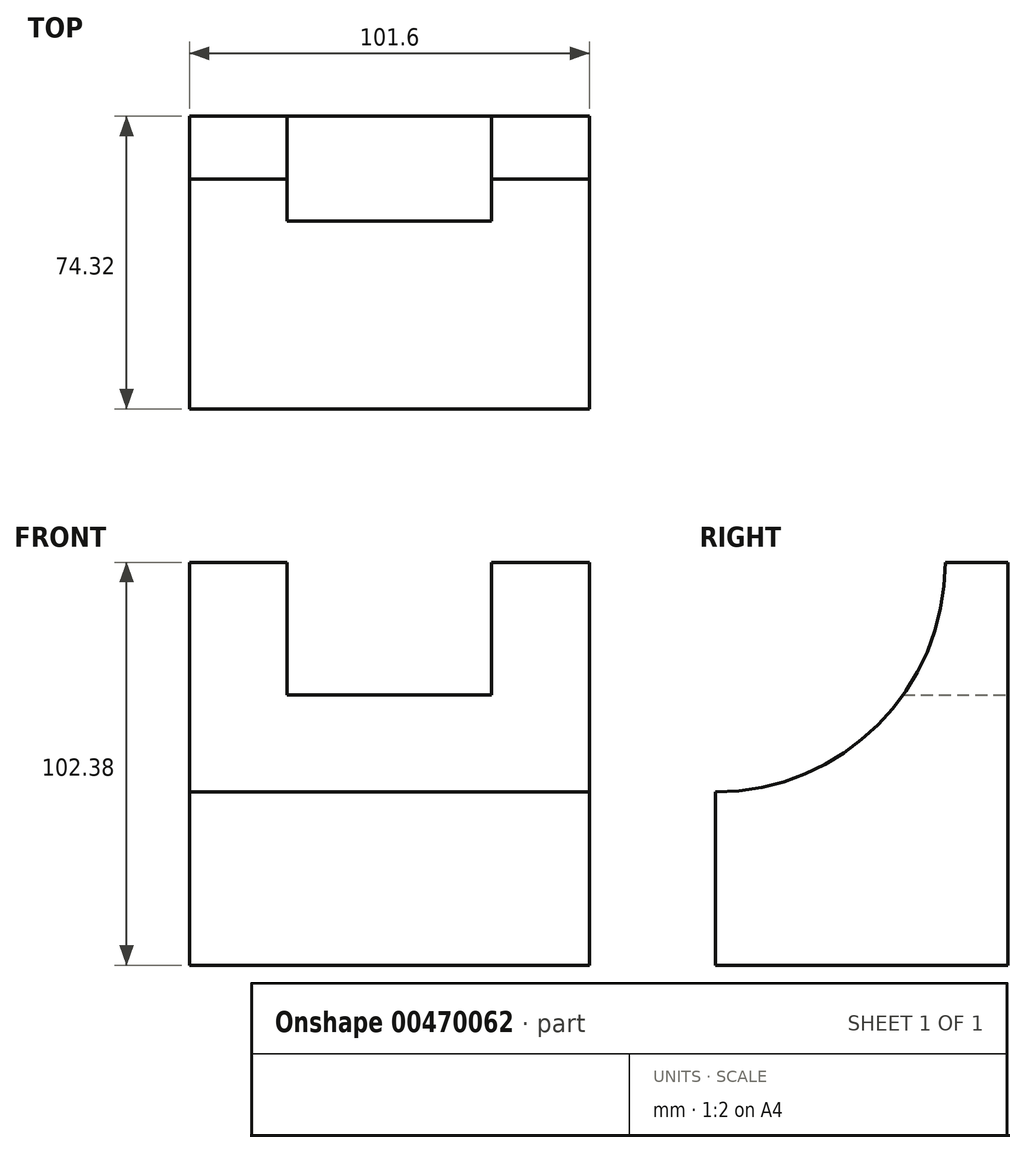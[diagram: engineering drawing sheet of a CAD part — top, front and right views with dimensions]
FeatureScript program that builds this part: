
annotation { "Feature Type Name" : "Feature", "Feature Type Description" : "" }
export const myFeature = defineFeature(function(context is Context, id is Id, definition is map)
    precondition{}
    {
        {
            var Q0;
            Q0=qCreatedBy(makeId("Right.planeOp"),FACE);
            var sketch = newSketch(context, id + "F0", { "sketchPlane" : qUnion([Q0])});
            skLineSegment(sketch, "E0.bottom", {"start": v(37.16, 51.2) * mm, "end": v(21.23, 51.2) * mm});
            skLineSegment(sketch, "E0.top", {"start": v(37.16, -51.2) * mm, "end": v(-37.16, -51.2) * mm});
            skLineSegment(sketch, "E0.left", {"start": v(37.16, 51.2) * mm, "end": v(37.16, -51.2) * mm});
            skLineSegment(sketch, "E0.right", {"start": v(-37.16, -7.2) * mm, "end": v(-37.16, -51.2) * mm});
            skPoint(sketch, "E0.middle", {"position": v(0, 0) * mm});
            skArc(sketch, "E1", {"start": v(21.23, 51.2) * mm, "mid": v(4.13, 9.9) * mm, "end": v(-37.16, -7.2) * mm});
            skSolve(sketch);
        }
        {
            var Q0;
            Q0 = qSketchRegion(id + "F0", true);
            extrude(context, id + "F1", {"entities" : qUnion([Q0]), "depth" : 101.6 * mm});
        }
        {
            var Q0;
            Q0=makeQuery(id+"F1.opExtrude","SWEPT_FACE",FACE,{"disambiguationData":[OSD([sQuery(id+"F0.wireOp",EDGE,"E0.left")])]});
            var sketch = newSketch(context, id + "F2", { "sketchPlane" : qUnion([Q0])});
            skLineSegment(sketch, "E2.bottom", {"start": v(-24.83, 17.44) * mm, "end": v(-76.77, 17.44) * mm});
            skLineSegment(sketch, "E2.top", {"start": v(-24.83, 84.94) * mm, "end": v(-76.77, 84.94) * mm});
            skLineSegment(sketch, "E2.left", {"start": v(-24.83, 17.44) * mm, "end": v(-24.83, 84.94) * mm});
            skLineSegment(sketch, "E2.right", {"start": v(-76.77, 17.44) * mm, "end": v(-76.77, 84.94) * mm});
            skPoint(sketch, "E2.middle", {"position": v(-50.8, 51.2) * mm});
            skLineSegment(sketch, "E3", {"start": v(-76.77, 51.2) * mm, "end": v(-24.83, 51.2) * mm});
            skSolve(sketch);
        }
        {
            var Q0;
            Q0 = qSketchRegion(id + "F2", true);
            extrude(context, id + "F3", {"entities" : qUnion([Q0]), "operationType" : NewBodyOperationType.REMOVE, "endBound" : BoundingType.THROUGH_ALL, "oppositeDirection" : true, "depth" : 25.4 * mm});
        }
    });
